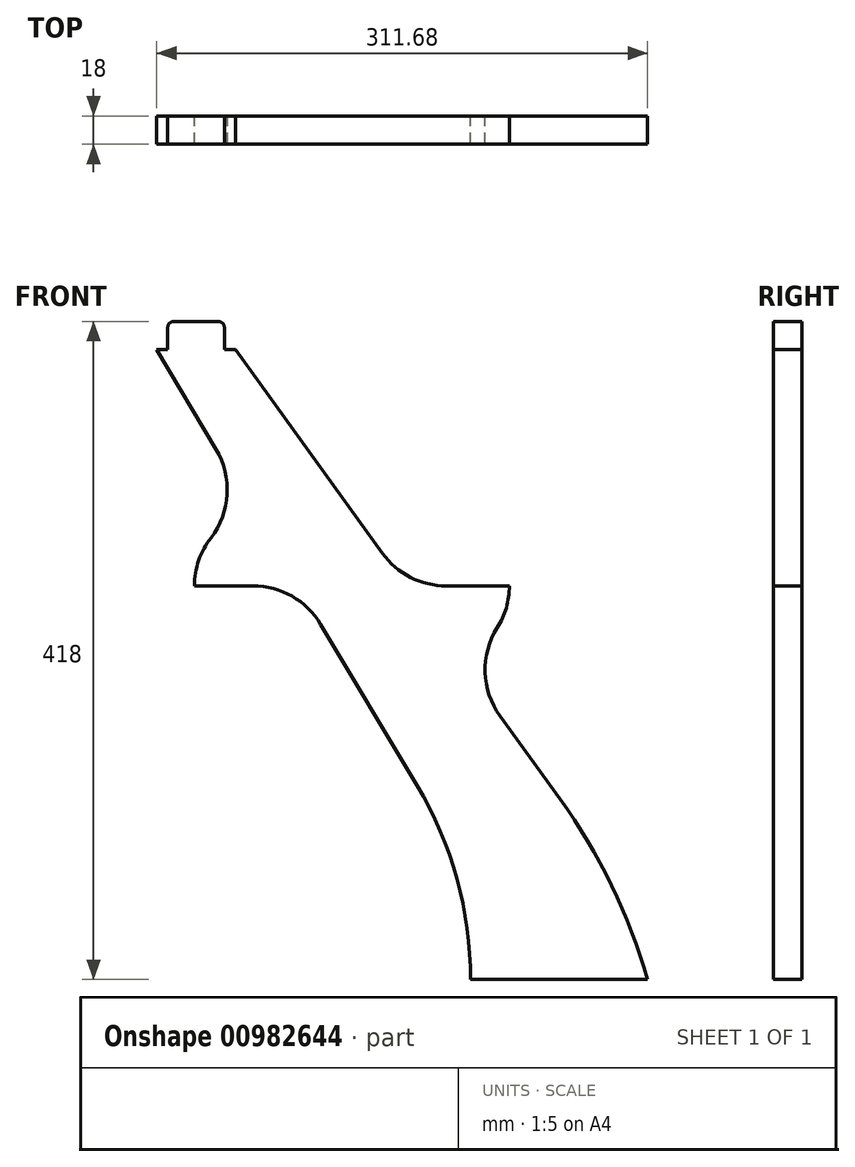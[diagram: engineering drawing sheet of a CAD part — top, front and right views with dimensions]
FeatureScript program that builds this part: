
annotation { "Feature Type Name" : "Feature", "Feature Type Description" : "" }
export const myFeature = defineFeature(function(context is Context, id is Id, definition is map)
    precondition{}
    {
        {
            var Q0;
            Q0=qCreatedBy(makeId("Front.planeOp"),FACE);
            var sketch = newSketch(context, id + "F0", { "sketchPlane" : qUnion([Q0])});
            skLineSegment(sketch, "E0.bottom", {"start": v(0, 0) * mm, "end": v(330, 0) * mm, "construction": true});
            skLineSegment(sketch, "E0.left", {"start": v(0, 0) * mm, "end": v(0, 400) * mm, "construction": true});
            skLineSegment(sketch, "E0.right", {"start": v(330, 0) * mm, "end": v(330, 400) * mm, "construction": true});
            skLineSegment(sketch, "E1.bottom", {"start": v(0, 436) * mm, "end": v(330, 436) * mm, "construction": true});
            skLineSegment(sketch, "E1.top", {"start": v(0, 400) * mm, "end": v(330, 400) * mm, "construction": true});
            skLineSegment(sketch, "E2", {"start": v(0, 400) * mm, "end": v(0, 436) * mm, "construction": true});
            skLineSegment(sketch, "E3", {"start": v(330, 436) * mm, "end": v(330, 400) * mm, "construction": true});
            skLineSegment(sketch, "E4", {"start": v(0, 250) * mm, "end": v(330, 250) * mm, "construction": true});
            skLineSegment(sketch, "E5", {"start": v(165, 0) * mm, "end": v(165, 436) * mm, "construction": true});
            skCircle(sketch, "E6", {"center": v(215, 250) * mm, "radius": 50 * mm, "construction": true});
            skLineSegment(sketch, "E7", {"start": v(330, 0) * mm, "end": v(165, 250) * mm, "construction": true});
            skLineSegment(sketch, "E8", {"start": v(165, 250) * mm, "end": v(66, 400) * mm, "construction": true});
            skLineSegment(sketch, "E9", {"start": v(91, 400) * mm, "end": v(297.14, 114.68) * mm, "construction": true});
            skLineSegment(sketch, "E10", {"start": v(280, 0) * mm, "end": v(352.68, 0) * mm});
            skCircle(sketch, "E11", {"center": v(299.6, 196.67) * mm, "radius": 50 * mm, "construction": true});
            skCircle(sketch, "E12", {"center": v(224.93, 300) * mm, "radius": 50 * mm, "construction": true});
            skLineSegment(sketch, "E13", {"start": v(280, 0) * mm, "end": v(41, 400) * mm, "construction": true});
            skCircle(sketch, "E14", {"center": v(115, 250) * mm, "radius": 50 * mm, "construction": true});
            skCircle(sketch, "E15", {"center": v(35.86, 311.13) * mm, "radius": 50 * mm, "construction": true});
            skCircle(sketch, "E16", {"center": v(102.25, 200) * mm, "radius": 50 * mm, "construction": true});
            skCircle(sketch, "E17", {"center": v(0, 0) * mm, "radius": 240.36 * mm, "construction": true});
            skLineSegment(sketch, "E18", {"start": v(280, 0) * mm, "end": v(240.36, 0) * mm});
            skLineSegment(sketch, "E19", {"start": v(297.14, 114.68) * mm, "end": v(259.06, 167.39) * mm});
            skLineSegment(sketch, "E20", {"start": v(206.34, 123.29) * mm, "end": v(145.18, 225.65) * mm});
            skLineSegment(sketch, "E21", {"start": v(65, 250) * mm, "end": v(102.25, 250) * mm});
            skArc(sketch, "E22", {"start": v(102.25, 250) * mm, "mid": v(126.93, 243.49) * mm, "end": v(145.18, 225.65) * mm});
            skArc(sketch, "E23", {"start": v(206.34, 123.29) * mm, "mid": v(231.7, 63.95) * mm, "end": v(240.36, 0) * mm});
            skArc(sketch, "E24", {"start": v(65, 250) * mm, "mid": v(67.68, 266.15) * mm, "end": v(75.43, 280.56) * mm});
            skArc(sketch, "E25", {"start": v(259.06, 167.39) * mm, "mid": v(249.62, 195.1) * mm, "end": v(257.3, 223.33) * mm});
            skArc(sketch, "E26", {"start": v(257.3, 223.33) * mm, "mid": v(263.04, 236.12) * mm, "end": v(265, 250) * mm});
            skArc(sketch, "E27", {"start": v(224.93, 250) * mm, "mid": v(202.18, 255.48) * mm, "end": v(184.4, 270.72) * mm});
            skLineSegment(sketch, "E28", {"start": v(265, 250) * mm, "end": v(224.93, 250) * mm});
            skArc(sketch, "E29", {"start": v(75.43, 280.56) * mm, "mid": v(85.77, 308.15) * mm, "end": v(78.78, 336.77) * mm});
            skLineSegment(sketch, "E30", {"start": v(184.4, 270.72) * mm, "end": v(91, 400) * mm});
            skLineSegment(sketch, "E31", {"start": v(78.78, 336.77) * mm, "end": v(41, 400) * mm});
            skLineSegment(sketch, "E32", {"start": v(48, 400) * mm, "end": v(48, 414) * mm});
            skLineSegment(sketch, "E33", {"start": v(84, 414) * mm, "end": v(84, 400) * mm});
            skLineSegment(sketch, "E34", {"start": v(52, 418) * mm, "end": v(80, 418) * mm});
            skPoint(sketch, "E35.visualSharp", {"position": v(48, 418) * mm});
            skArc(sketch, "E35.filletArc", {"start": v(52, 418) * mm, "mid": v(49.17, 416.83) * mm, "end": v(48, 414) * mm});
            skPoint(sketch, "E36.visualSharp", {"position": v(84, 418) * mm});
            skArc(sketch, "E36.filletArc", {"start": v(84, 414) * mm, "mid": v(82.83, 416.83) * mm, "end": v(80, 418) * mm});
            skLineSegment(sketch, "E37", {"start": v(48, 400) * mm, "end": v(41, 400) * mm});
            skLineSegment(sketch, "E38", {"start": v(84, 400) * mm, "end": v(91, 400) * mm});
            skCircle(sketch, "E39", {"center": v(0, -100) * mm, "radius": 366.58 * mm, "construction": true});
            skArc(sketch, "E40", {"start": v(352.68, 0) * mm, "mid": v(329.93, 59.77) * mm, "end": v(297.14, 114.68) * mm});
            skPoint(sketch, "E41.orphan", {"position": v(380, 0) * mm});
            skSolve(sketch);
        }
        {
            var Q0;
            Q0 = qSketchRegion(id + "F0", true);
            extrude(context, id + "F1", {"entities" : qUnion([Q0]), "depth" : 18 * mm, "offsetDistance" : 25 * mm});
        }
    });
